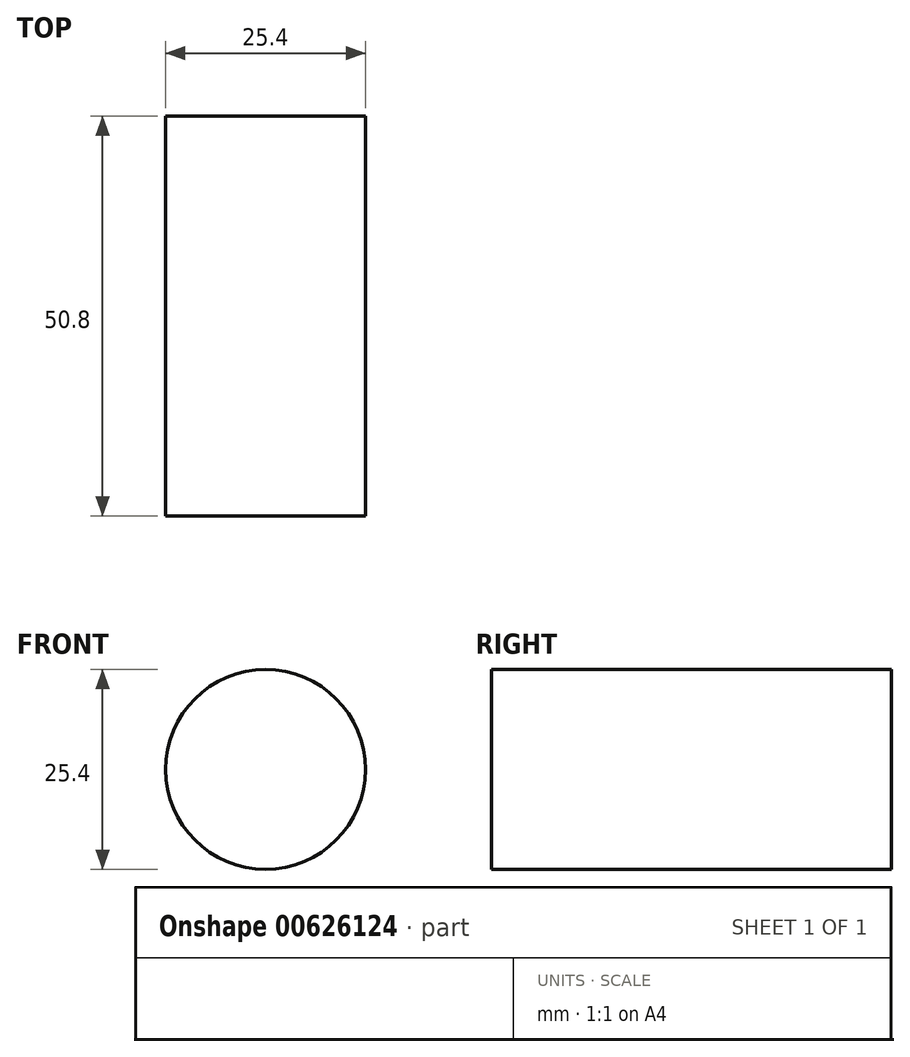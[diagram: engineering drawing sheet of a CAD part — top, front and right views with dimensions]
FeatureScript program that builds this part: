
annotation { "Feature Type Name" : "Feature", "Feature Type Description" : "" }
export const myFeature = defineFeature(function(context is Context, id is Id, definition is map)
    precondition{}
    {
        {
            var Q0;
            Q0=qCreatedBy(makeId("Front.planeOp"),FACE);
            var sketch = newSketch(context, id + "F0", { "sketchPlane" : qUnion([Q0])});
            skCircle(sketch, "E0", {"center": v(0, 0) * mm, "radius": 12.7 * mm});
            skSolve(sketch);
        }
        {
            var Q0;
            Q0 = qSketchRegion(id + "F0", false);
            extrude(context, id + "F1", {"entities" : qUnion([Q0]), "depth" : 25.4 * mm});
        }
        {
            var Q0;
            Q0=makeQuery(id+"F1.opExtrude","CAP_FACE",FACE,{"disambiguationData":[OSD([sQuery(id+"F0.wireOp",EDGE,"E0")])],"isStart":false});
            var sketch = newSketch(context, id + "F2", { "sketchPlane" : qUnion([Q0])});
            skCircle(sketch, "E0", {"center": v(0, 0) * mm, "radius": 12.7 * mm});
            skSolve(sketch);
        }
        {
            var Q0;
            Q0 = qSketchRegion(id + "F2", false);
            extrude(context, id + "F3", {"entities" : qUnion([Q0]), "operationType" : NewBodyOperationType.ADD, "depth" : 25.4 * mm});
        }
    });
